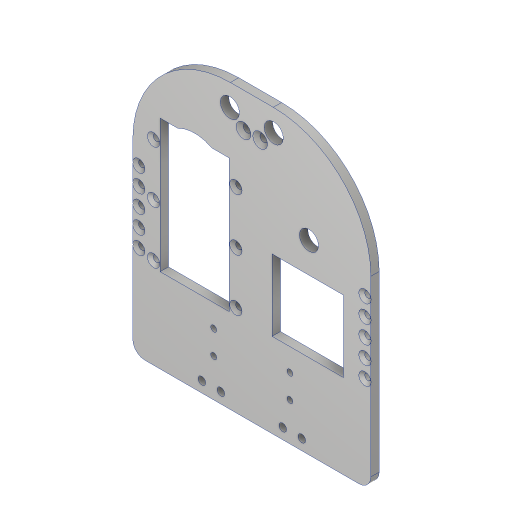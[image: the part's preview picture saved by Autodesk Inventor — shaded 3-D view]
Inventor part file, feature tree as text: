
AUTODESK INVENTOR PART (.ipt)
format: ipt  version: 2023.2 (Build 272271000, 271)  size: 443,392 bytes
history: native  units: mm
features: extrude x19, sketch x19, chamfer x4, projected_geometry x4, fillet x3, other x1
ambient origin geometry x8: Origin, YZ Plane, XZ Plane, XY Plane, X Axis, Y Axis, Z Axis, Center Point
bodies: Body1 (feature_tree)
feature tree (50):
  other  "솔리드1"
  extrude  "돌출1"  Depth=100.02mm
  extrude  "돌출2"  Depth=50.01mm
  extrude  "돌출3"  Depth=94.0mm
  extrude  "돌출4"  Depth=3.5mm TaperAngle=0.0deg
  extrude  "돌출5"  Depth=28.0mm
  extrude  "돌출6"  Depth=24.01mm
  chamfer  "모따기1"  Distance=53.1mm
  extrude  "돌출7"  Depth=4.0mm TaperAngle=0.0deg
  fillet  "모깎기1"  Radius=10.4mm
  extrude  "돌출8"  Depth=55.9mm
  chamfer  "모따기2"  Distance=29.04mm
  extrude  "돌출9"  Depth=14.52mm
  chamfer  "모따기3"  Distance=4.0mm
  extrude  "돌출10"  Depth=30.0mm
  extrude  "돌출11"  Depth=4.0mm TaperAngle=0.0deg
  fillet  "모깎기2"  Radius=3.41mm
  extrude  "돌출13"  Depth=2.7mm
  chamfer  "모따기5"  Distance=2.7mm
  extrude  "돌출17"  Depth=2.7mm
  extrude  "돌출18"  Depth=2.7mm
  extrude  "돌출19"  Depth=2.7mm
  fillet  "모깎기3"  Radius=2.7mm
  extrude  "돌출20"  Depth=2.7mm
  extrude  "돌출21"  Depth=2.7mm
  extrude  "돌출22"  Depth=4.0mm TaperAngle=0.0deg
  extrude  "돌출15"  Depth=48.02mm
  sketch  "스케치1"
  sketch  "스케치2"
  sketch  "스케치3"
  sketch  "스케치4"
  sketch  "스케치5"
  sketch  "스케치6"
  sketch  "스케치7"
  sketch  "스케치8"
  sketch  "스케치9"
  sketch  "스케치10"
  sketch  "스케치11"
  sketch  "스케치13"
  sketch  "스케치15"
  sketch  "스케치17"
  sketch  "스케치19"
  projected_geometry  "투영된 루프1"
  sketch  "스케치20"
  projected_geometry  "투영된 루프2"
  sketch  "스케치21"
  projected_geometry  "투영된 루프3"
  sketch  "스케치22"
  projected_geometry  "투영된 루프4"
  sketch  "스케치23"
